# Revit family: 03419473
name_source: partatom
category: Plumbing Fixtures
units: mm (PartAtom-declared; Revit-internal decimal feet)

## family parameters
Always vertical = Yes
Cut with Voids When Loaded = No
OmniClass Number = 23.45.55.00
OmniClass Title = Sanitary Faucets, Wastes
Part Type = Normal
Room Calculation Point = No
Round Connector Dimension = Use Diameter
Shared = No
Work Plane-Based = No

## types (1)
- 03419473 Cover part for bath and shower faucet, 72 mm
    2D/3D/BIM Files URL = http://static.hansa.com
    3D View = https://static.hansa.com
    Advanced Features = Inner body made of DZR brass
    Ambience photo = http://static.hansa.com
    AssetType = Fixed
    BIMObjectName = 03419473
    Backflow Prevention EN1717 = EB
    BodyMaterial = Brass
    Brand = HANSA
    Catalog Drawing URL = http://static.hansa.com
    Category = Bathtub & Shower
    CloseOffRating = 0
    Color = Chrome
    Concealed Parts = Round rosette
    Default Elevation = 0 mm  [stored 0 ft]
    Dimension Drawing URL = http://static.hansa.com
    DurationUnit = Year
    EAN Number = 4057304014642
    EN Standard = EN 817, EN 1112, EN 1113
    ETIM Class Number = EC010862 Bath mixing tap
    FDV Document URL = http://www.hansa.com
    FaucetMainMaterial = Brass
    Features = Trim Kit;Single-lever
    Finish = Polished
    Flow Drawing URL = http://static.hansa.com
    Flow Rate At 300kPa = 0.2 L/s
    FlowCoefficient = 0
    Group = Bath faucet
    IfcExportAs = IfcValveType
    IfcExportType = FAUCET
    Installation Type = Rim mounted
    Installation and Maintenance Guide URL = http://static.hansa.com
    Interactive AR View URL = https://static.hansa.com
    Lever Handle = Single operating lever/handle;Hot/Cold symbols
    Manufacturer = HANSA
    ManufacturerName = HANSA
    ManufacturerURL = http://www.hansa.com
    Market = International;Germany;Austria;Belgium;Netherlands;France;Czech Republic;Slovakia;Italy;Spain
    Material = Brass
    Max. Hot Water Supply = 80 °C
    Mechanical Parts = ø 40 mm ceramic cartridge for flow and temperature control;Non-return valve(s);Litter filter(s)
    Mobile Product Information URL = http://mpi.hansa.com
    Model = 03419473 Cover part for bath and shower faucet, 72 mm
    ModelReference = 03419473
    Mounting Holes = 3 hole
    NBSDescription = Water supply fittings for baths
    NBSReference = 45-35-70/315
    Name = 03419473 Cover part for bath and shower faucet, 72 mm
    Name_en = 03419473 Cover part for bath and shower faucet, 72 mm
    NominalDepth = 226 mm
    NominalHeight = 279 mm
    NominalWidth = 456 mm
    Product Code = 03419473
    Product Family = HANSARONDA
    Product Image URL = http://static.hansa.com
    Product URL = http://static.hansa.com
    Sales Package dimensions (LxWxH) = 570 x 505 x 135
    Shape = Sculptured
    Shower Parts = Hand shower;Shower hose (1750 mm)
    Shower Spray = Intense
    Shower Spray Number = 1 shower spray
    Size = 455x225x280 mm
    Spare-Part Information URL = http://static.hansa.com
    Surface treatment = Chrome
    Technical DataSheet URL = http://www.hansa.com
    UNSPSC Class Number = 30181700 Faucets or taps
    URL Declaration Of Performance (DOP) = http://static.hansa.com
    URL Declaration of Asbestos = http://static.hansa.com
    URL Declaration of Conformity = http://static.hansa.com
    URL Declaration of SCIP = http://static.hansa.com
    URL EU Packaging Declaration = http://static.hansa.com
    URL EcoLabel Declaration = http://static.hansa.com
    URL Materials Declaration = http://www.hansa.com
    URL REACH = http://static.hansa.com
    URL UWL = http://static.hansa.com
    Uniclass2 = Pr_40_30_96_07
    Uniclass2015Description = Bath manual water supply sets
    Uniclass2015Reference = Pr_40_20_87_07
    Version = 1
    VersionDate = 01/06/2023
    Warranty Information URL = http://warranty.hansa.com
    WarrantyDescription = http://warranty.hansa.com
    WarrantyDurationUnit = Year
    Working Pressure = 50 - 1000 kPa

note: [stored X ft] marks values corroborated as IEEE doubles in the binary element streams (Revit-internal decimal feet)

## geometry (parser evidence)
native form markers: Sweep x6
no freeform markers — native parametric forms only
